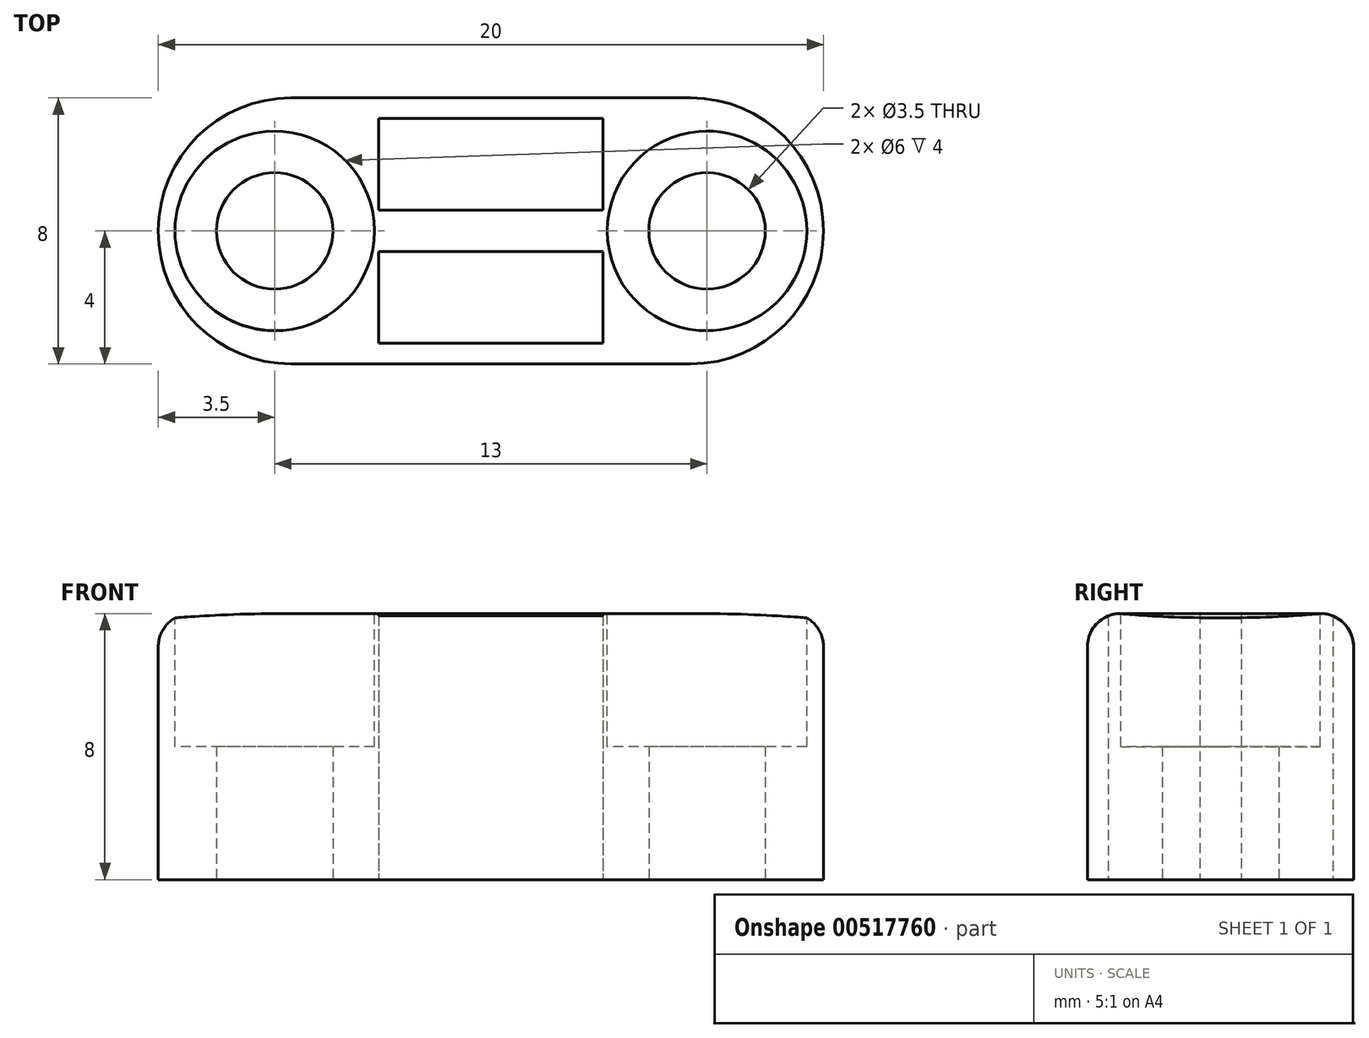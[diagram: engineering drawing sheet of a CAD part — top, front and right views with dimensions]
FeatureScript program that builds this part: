
annotation { "Feature Type Name" : "Feature", "Feature Type Description" : "" }
export const myFeature = defineFeature(function(context is Context, id is Id, definition is map)
    precondition{}
    {
        {
            var Q0;
            Q0=qCreatedBy(makeId("Top.planeOp"),FACE);
            var sketch = newSketch(context, id + "F0", { "sketchPlane" : qUnion([Q0])});
            skLineSegment(sketch, "E0.bottom", {"start": v(6, 4) * mm, "end": v(-6, 4) * mm});
            skLineSegment(sketch, "E0.top", {"start": v(6, -4) * mm, "end": v(-6, -4) * mm});
            skPoint(sketch, "E0.middle", {"position": v(0, 0) * mm});
            skLineSegment(sketch, "E1", {"start": v(0, 4) * mm, "end": v(0, 0) * mm, "construction": true});
            skLineSegment(sketch, "E2", {"start": v(0, -4) * mm, "end": v(0, 0) * mm, "construction": true});
            skLineSegment(sketch, "E3.bottom", {"start": v(3.38, 0.63) * mm, "end": v(-3.37, 0.63) * mm});
            skLineSegment(sketch, "E3.top", {"start": v(3.38, 3.38) * mm, "end": v(-3.37, 3.38) * mm});
            skLineSegment(sketch, "E3.left", {"start": v(3.38, 0.63) * mm, "end": v(3.38, 3.38) * mm});
            skLineSegment(sketch, "E3.right", {"start": v(-3.37, 0.63) * mm, "end": v(-3.37, 3.38) * mm});
            skPoint(sketch, "E3.middle", {"position": v(0, 2) * mm});
            skLineSegment(sketch, "E4.bottom", {"start": v(3.38, -3.37) * mm, "end": v(-3.37, -3.37) * mm});
            skLineSegment(sketch, "E4.top", {"start": v(3.38, -0.62) * mm, "end": v(-3.37, -0.62) * mm});
            skLineSegment(sketch, "E4.left", {"start": v(3.38, -3.37) * mm, "end": v(3.38, -0.62) * mm});
            skLineSegment(sketch, "E4.right", {"start": v(-3.37, -3.37) * mm, "end": v(-3.37, -0.62) * mm});
            skPoint(sketch, "E4.middle", {"position": v(0, -2) * mm});
            skLineSegment(sketch, "E5", {"start": v(0, 0) * mm, "end": v(-10, 0) * mm, "construction": true});
            skLineSegment(sketch, "E6", {"start": v(0, 0) * mm, "end": v(10, 0) * mm, "construction": true});
            skLineSegment(sketch, "E7", {"start": v(-6.5, 8.35) * mm, "end": v(-6.5, -5.9) * mm, "construction": true});
            skLineSegment(sketch, "E8", {"start": v(6.5, 7.82) * mm, "end": v(6.5, -6.48) * mm, "construction": true});
            skCircle(sketch, "E9", {"center": v(-6.5, 0) * mm, "radius": 1.75 * mm});
            skCircle(sketch, "E10", {"center": v(6.5, 0) * mm, "radius": 1.75 * mm});
            skPoint(sketch, "E11", {"position": v(-6, 0) * mm});
            skPoint(sketch, "E12", {"position": v(6, 0) * mm});
            skArc(sketch, "E13", {"start": v(-6, 4) * mm, "mid": v(-10, 0) * mm, "end": v(-6, -4) * mm});
            skArc(sketch, "E14", {"start": v(6, 4) * mm, "mid": v(10, 0) * mm, "end": v(6, -4) * mm});
            skPoint(sketch, "E15.orphan", {"position": v(10, 4) * mm});
            skPoint(sketch, "E16.orphan", {"position": v(10, -4) * mm});
            skPoint(sketch, "E17.orphan", {"position": v(-10, 4) * mm});
            skPoint(sketch, "E18.orphan", {"position": v(-10, -4) * mm});
            skSolve(sketch);
        }
        {
            var Q0;
            Q0 = qSketchRegion(id + "F0", true);
            extrude(context, id + "F1", {"entities" : qUnion([Q0]), "depth" : 8 * mm, "offsetDistance" : 25 * mm});
        }
        {
            var Q0;
            Q0=makeQuery(id+"F1.opExtrude","CAP_FACE",FACE,{"disambiguationData":[OSD([sQuery(id+"F0.wireOp",EDGE,"E0.bottom"),sQuery(id+"F0.wireOp",EDGE,"E0.top"),sQuery(id+"F0.wireOp",EDGE,"E3.bottom"),sQuery(id+"F0.wireOp",EDGE,"E3.top"),sQuery(id+"F0.wireOp",EDGE,"E3.left"),sQuery(id+"F0.wireOp",EDGE,"E3.right"),sQuery(id+"F0.wireOp",EDGE,"E4.bottom"),sQuery(id+"F0.wireOp",EDGE,"E4.top"),sQuery(id+"F0.wireOp",EDGE,"E4.left"),sQuery(id+"F0.wireOp",EDGE,"E4.right"),sQuery(id+"F0.wireOp",EDGE,"E9"),sQuery(id+"F0.wireOp",EDGE,"E10"),sQuery(id+"F0.wireOp",EDGE,"E13"),sQuery(id+"F0.wireOp",EDGE,"E14")])],"isStart":false});
            var sketch = newSketch(context, id + "F2", { "sketchPlane" : qUnion([Q0])});
            skCircle(sketch, "E19.0", {"center": v(-6.5, 0) * mm, "radius": 1.75 * mm});
            skCircle(sketch, "E20.0", {"center": v(6.5, 0) * mm, "radius": 1.75 * mm});
            skCircle(sketch, "E21", {"center": v(-6.5, 0) * mm, "radius": 3 * mm});
            skCircle(sketch, "E22", {"center": v(6.5, 0) * mm, "radius": 3 * mm});
            skSolve(sketch);
        }
        {
            var Q0;
            Q0 = qSketchRegion(id + "F2", true);
            extrude(context, id + "F3", {"entities" : qUnion([Q0]), "operationType" : NewBodyOperationType.REMOVE, "oppositeDirection" : true, "depth" : 4 * mm, "offsetDistance" : 25 * mm});
        }
        {
            var Q0;
            Q0=makeQuery(id+"F1.opExtrude","CAP_EDGE",EDGE,{"disambiguationData":[OSD([sQuery(id+"F0.wireOp",EDGE,"E14")])],"isStart":false});
            fillet(context, id + "F4", {"entities" : qUnion([Q0]), "radius" : 1 * mm, "tangentPropagation" : true, "allowEdgeOverflow" : false});
        }
    });
